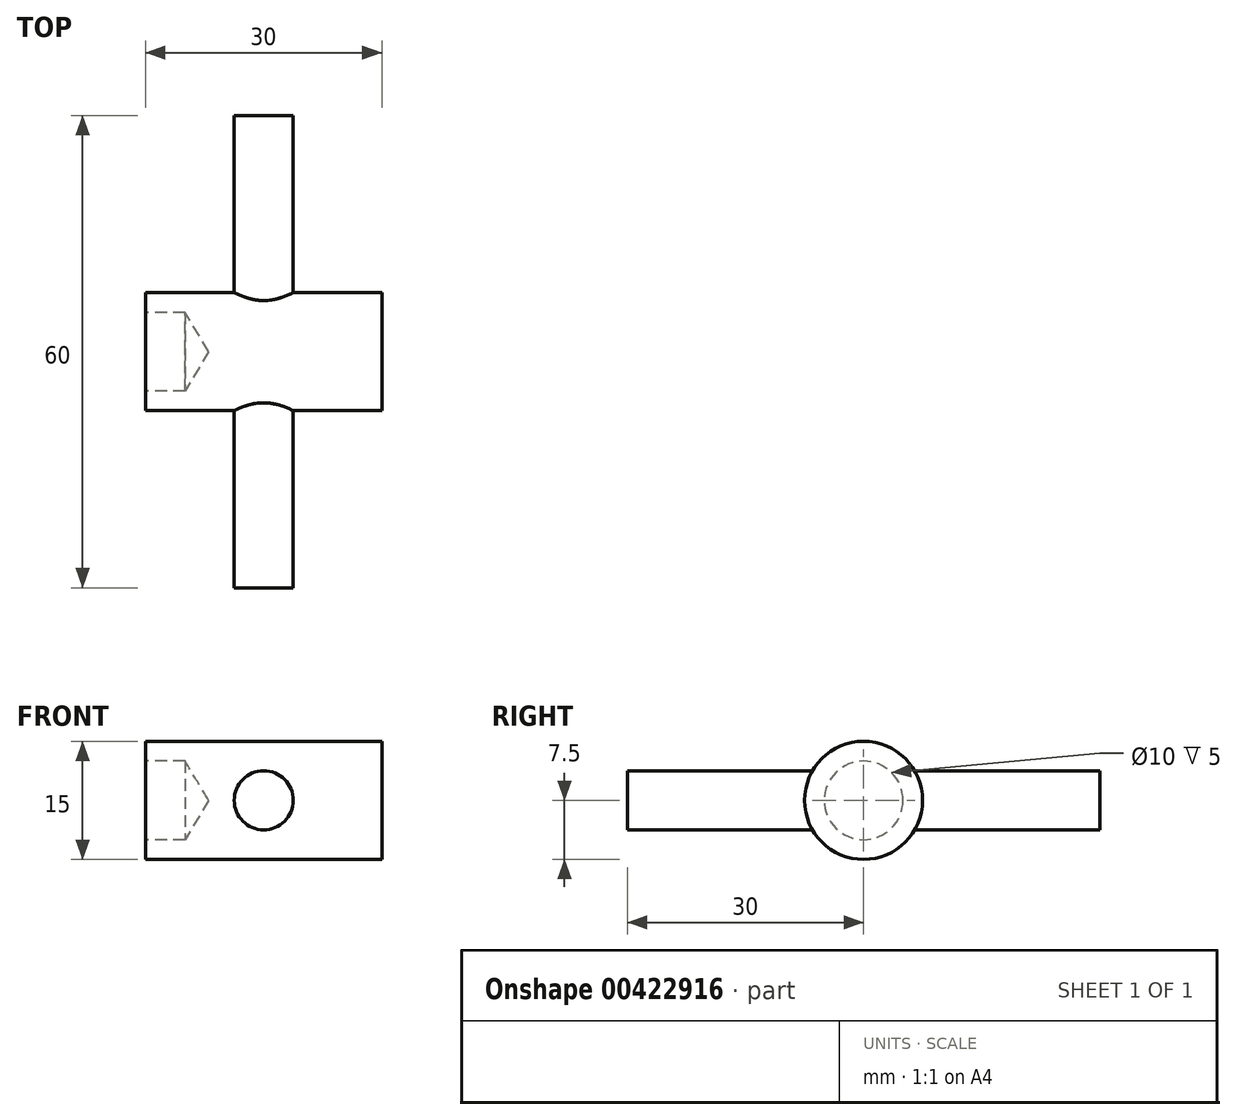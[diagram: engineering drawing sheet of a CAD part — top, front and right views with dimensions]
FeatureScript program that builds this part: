
annotation { "Feature Type Name" : "Feature", "Feature Type Description" : "" }
export const myFeature = defineFeature(function(context is Context, id is Id, definition is map)
    precondition{}
    {
        {
            var Q0;
            Q0=qCreatedBy(makeId("Front.planeOp"),FACE);
            var sketch = newSketch(context, id + "F0", { "sketchPlane" : qUnion([Q0])});
            skLineSegment(sketch, "E0.bottom", {"start": v(0, 0) * mm, "end": v(30, 0) * mm});
            skLineSegment(sketch, "E0.top", {"start": v(0, 7.5) * mm, "end": v(30, 7.5) * mm});
            skLineSegment(sketch, "E0.left", {"start": v(0, 0) * mm, "end": v(0, 7.5) * mm});
            skLineSegment(sketch, "E0.right", {"start": v(30, 0) * mm, "end": v(30, 7.5) * mm});
            skLineSegment(sketch, "E1", {"start": v(0, 0) * mm, "end": v(15, 0) * mm, "construction": true});
            skCircle(sketch, "E2", {"center": v(15, 0) * mm, "radius": 3.75 * mm});
            skSolve(sketch);
        }
        {
            var Q0;
            Q0 = qSketchRegion(id + "F0", true);
            var Q1;
            Q1=sQuery(id+"F0.wireOp",EDGE,"E0.bottom");
            revolve(context, id + "F1", {"entities" : qUnion([Q0]), "axis" : qUnion([Q1]), "revolveType" : RevolveType.FULL});
        }
        {
            var Q0;
            Q0=makeQuery(id+"F1.opRevolve","SWEPT_FACE",FACE,{"disambiguationData":[OSD([sQuery(id+"F0.wireOp",EDGE,"E0.left")])]});
            var sketch = newSketch(context, id + "F2", { "sketchPlane" : qUnion([Q0])});
            skPoint(sketch, "E3", {"position": v(0, 0) * mm});
            skSolve(sketch);
        }
        {
            var Q0;
            Q0=sQuery(id+"F2.wireOp",VERTEX,"E3");
            var Q1;
            Q1=makeQuery(id+"F1.opRevolve","SWEPT_BODY",BODY,{"disambiguationData":[OSD([sQuery(id+"F0.wireOp",EDGE,"E0.bottom"),sQuery(id+"F0.wireOp",EDGE,"E0.top"),sQuery(id+"F0.wireOp",EDGE,"E0.left"),sQuery(id+"F0.wireOp",EDGE,"E0.right")])]});
            hole(context, id + "F3", {"style" : HoleStyle.SIMPLE, "endStyle" : HoleEndStyle.BLIND, "holeDiameter" : 10 * mm, "holeDepth" : 5 * mm, "isTappedThrough" : true, "tappedDepth" : 12 * mm, "tapClearance" : 3, "startFromSketch" : true, "locations" : qUnion([Q0]), "scope" : qUnion([Q1])});
        }
        {
            var Q0;
            {var subQ0=sQuery(id+"F0.wireOp",EDGE,"E2");var subQ1=sQuery(id+"F0.wireOp",EDGE,"E0.bottom");var subQ2=makeQuery(id+"F0.imprint","INTERSECT",VERTEX,{"disambiguationData":[OD(0.0)],"derivedFrom":[subQ1,subQ0]});Q0=makeQuery(id+"F0.imprint","IMPRINT",FACE,{"disambiguationData":[TD([[makeQuery(id+"F0.imprint","IMPRINT",EDGE,{"disambiguationData":[TD([[subQ2,-1.0]])],"derivedFrom":subQ1}),1.0]])]});}
            var Q1;
            {var subQ0=sQuery(id+"F0.wireOp",EDGE,"E2");var subQ1=sQuery(id+"F0.wireOp",EDGE,"E0.bottom");var subQ2=makeQuery(id+"F0.imprint","INTERSECT",VERTEX,{"disambiguationData":[OD(0.0)],"derivedFrom":[subQ1,subQ0]});Q1=makeQuery(id+"F0.imprint","IMPRINT",FACE,{"disambiguationData":[TD([[makeQuery(id+"F0.imprint","IMPRINT",EDGE,{"disambiguationData":[TD([[subQ2,-1.0]])],"derivedFrom":subQ1}),-1.0]])]});}
            extrude(context, id + "F4", {"entities" : qUnion([Q0, Q1]), "operationType" : NewBodyOperationType.ADD, "endBound" : BoundingType.SYMMETRIC, "depth" : 60 * mm});
        }
    });
